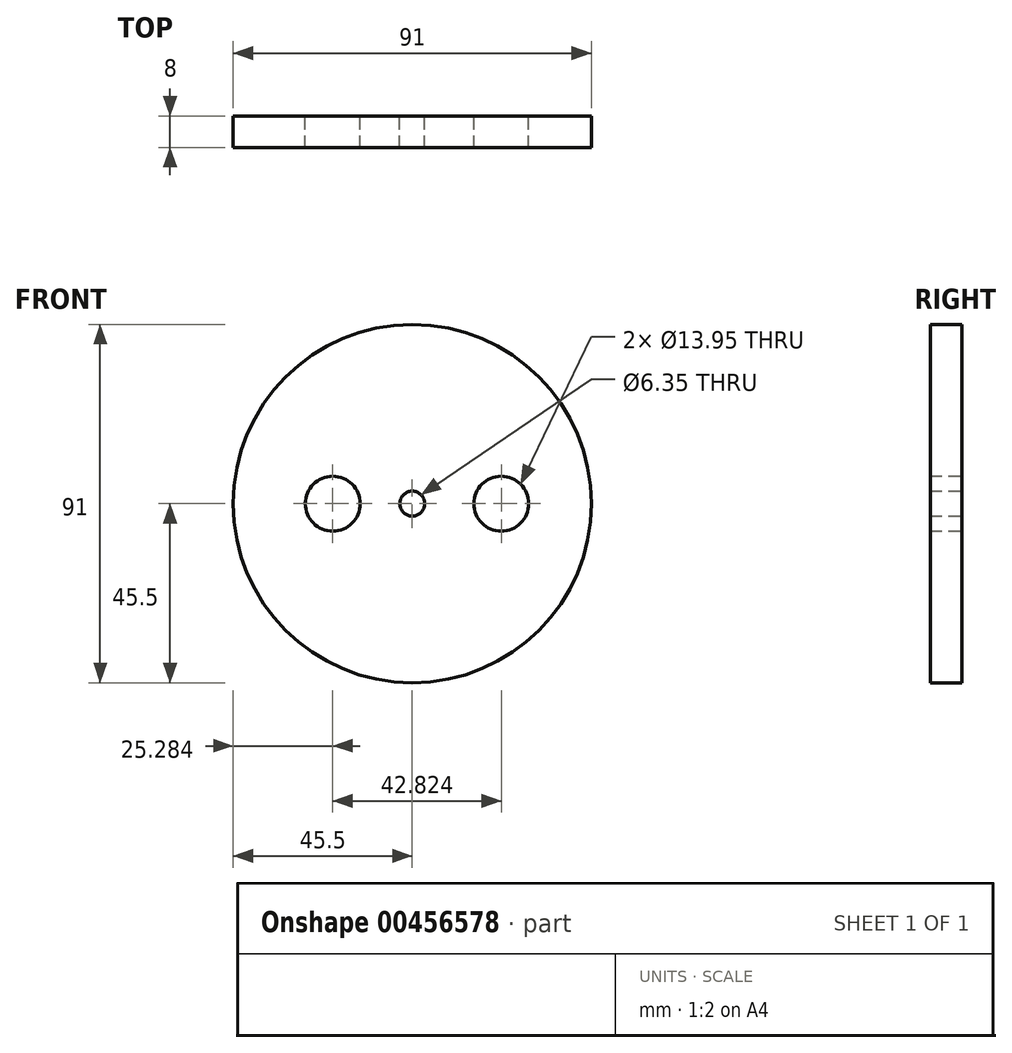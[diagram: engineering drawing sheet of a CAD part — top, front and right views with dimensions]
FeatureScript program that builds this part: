
annotation { "Feature Type Name" : "Feature", "Feature Type Description" : "" }
export const myFeature = defineFeature(function(context is Context, id is Id, definition is map)
    precondition{}
    {
        {
            var Q0;
            Q0=qCreatedBy(makeId("Front.planeOp"),FACE);
            var sketch = newSketch(context, id + "F0", { "sketchPlane" : qUnion([Q0])});
            skCircle(sketch, "E0", {"center": v(0, 0) * mm, "radius": 45.5 * mm});
            skSolve(sketch);
        }
        {
            var Q0;
            Q0=qCreatedBy(makeId("Front.planeOp"),FACE);
            var sketch = newSketch(context, id + "F1", { "sketchPlane" : qUnion([Q0])});
            skCircle(sketch, "E1", {"center": v(0, 0) * mm, "radius": 3.17 * mm});
            skSolve(sketch);
        }
        {
            var Q0;
            Q0 = qSketchRegion(id + "F0", true);
            extrude(context, id + "F2", {"entities" : qUnion([Q0]), "depth" : 8 * mm, "offsetDistance" : 25 * mm});
        }
        {
            var Q0;
            Q0 = qSketchRegion(id + "F1", true);
            extrude(context, id + "F3", {"entities" : qUnion([Q0]), "operationType" : NewBodyOperationType.REMOVE, "endBound" : BoundingType.THROUGH_ALL, "depth" : 25 * mm, "offsetDistance" : 25 * mm});
        }
        {
            var Q0;
            Q0=qCreatedBy(makeId("Front.planeOp"),FACE);
            var sketch = newSketch(context, id + "F4", { "sketchPlane" : qUnion([Q0])});
            skCircle(sketch, "E2", {"center": v(-20.22, 0) * mm, "radius": 6.97 * mm});
            skCircle(sketch, "E3", {"center": v(22.6, 0) * mm, "radius": 6.97 * mm});
            skSolve(sketch);
        }
        {
            var Q0;
            Q0 = qSketchRegion(id + "F4", true);
            extrude(context, id + "F5", {"entities" : qUnion([Q0]), "operationType" : NewBodyOperationType.REMOVE, "depth" : 25 * mm, "offsetDistance" : 25 * mm});
        }
    });
